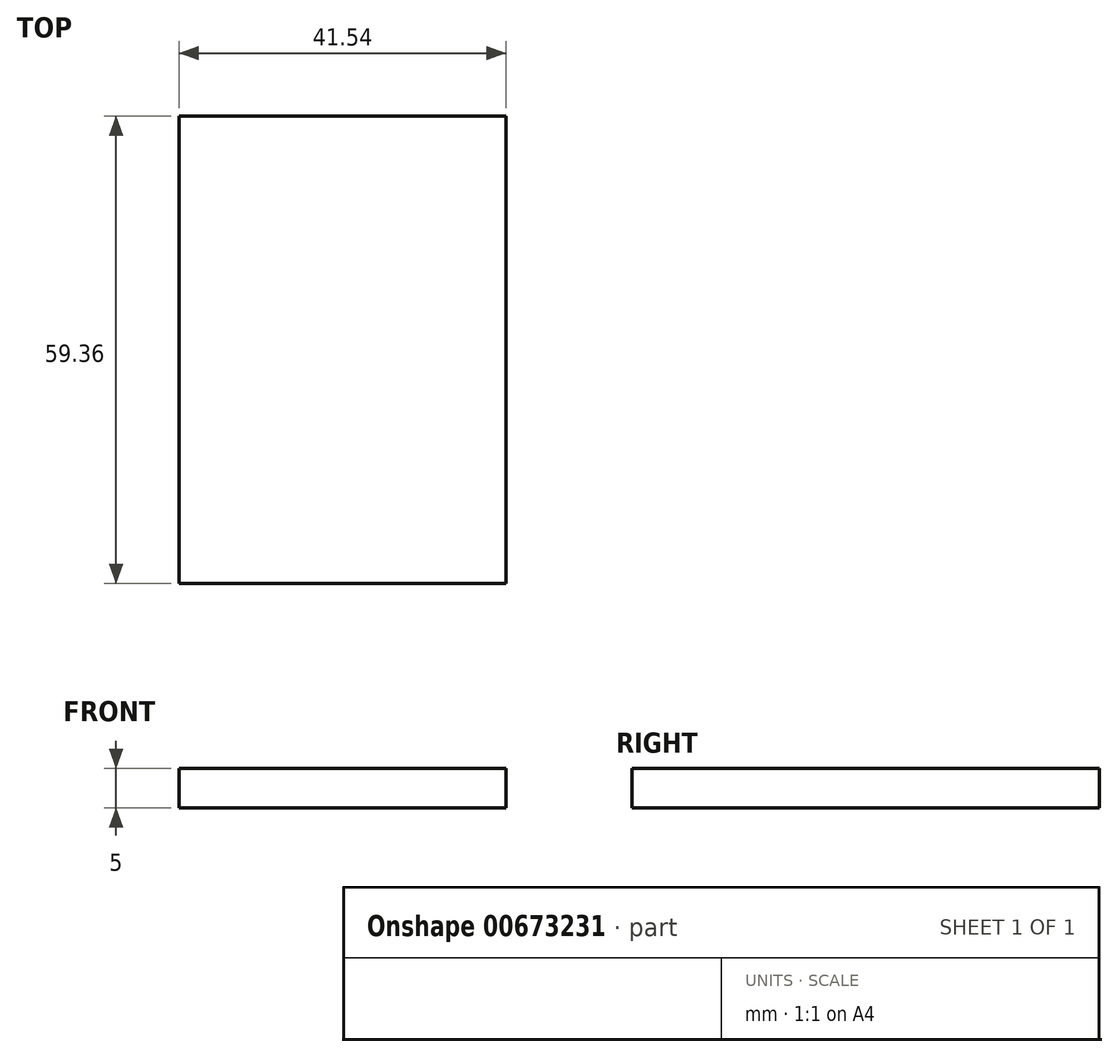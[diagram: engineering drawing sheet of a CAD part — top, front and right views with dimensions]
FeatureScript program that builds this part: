
annotation { "Feature Type Name" : "Feature", "Feature Type Description" : "" }
export const myFeature = defineFeature(function(context is Context, id is Id, definition is map)
    precondition{}
    {
        {
            var Q0;
            Q0=qCreatedBy(makeId("Top.planeOp"),FACE);
            var sketch = newSketch(context, id + "F0", { "sketchPlane" : qUnion([Q0])});
            skLineSegment(sketch, "E0.bottom", {"start": v(0, 0) * mm, "end": v(41.54, 0) * mm});
            skLineSegment(sketch, "E0.top", {"start": v(0, 59.36) * mm, "end": v(41.54, 59.36) * mm});
            skLineSegment(sketch, "E0.left", {"start": v(0, 0) * mm, "end": v(0, 59.36) * mm});
            skLineSegment(sketch, "E0.right", {"start": v(41.54, 0) * mm, "end": v(41.54, 59.36) * mm});
            skSolve(sketch);
        }
        {
            var Q0;
            Q0=makeQuery(id+"F0.imprint","IMPRINT",FACE,{"disambiguationData":[TD([[makeQuery(id+"F0.imprint","IMPRINT",EDGE,{"derivedFrom":sQuery(id+"F0.wireOp",EDGE,"E0.bottom")}),1.0]])]});
            extrude(context, id + "F1", {"entities" : qUnion([Q0]), "depth" : 5 * mm, "offsetDistance" : 25.4 * mm});
        }
    });
